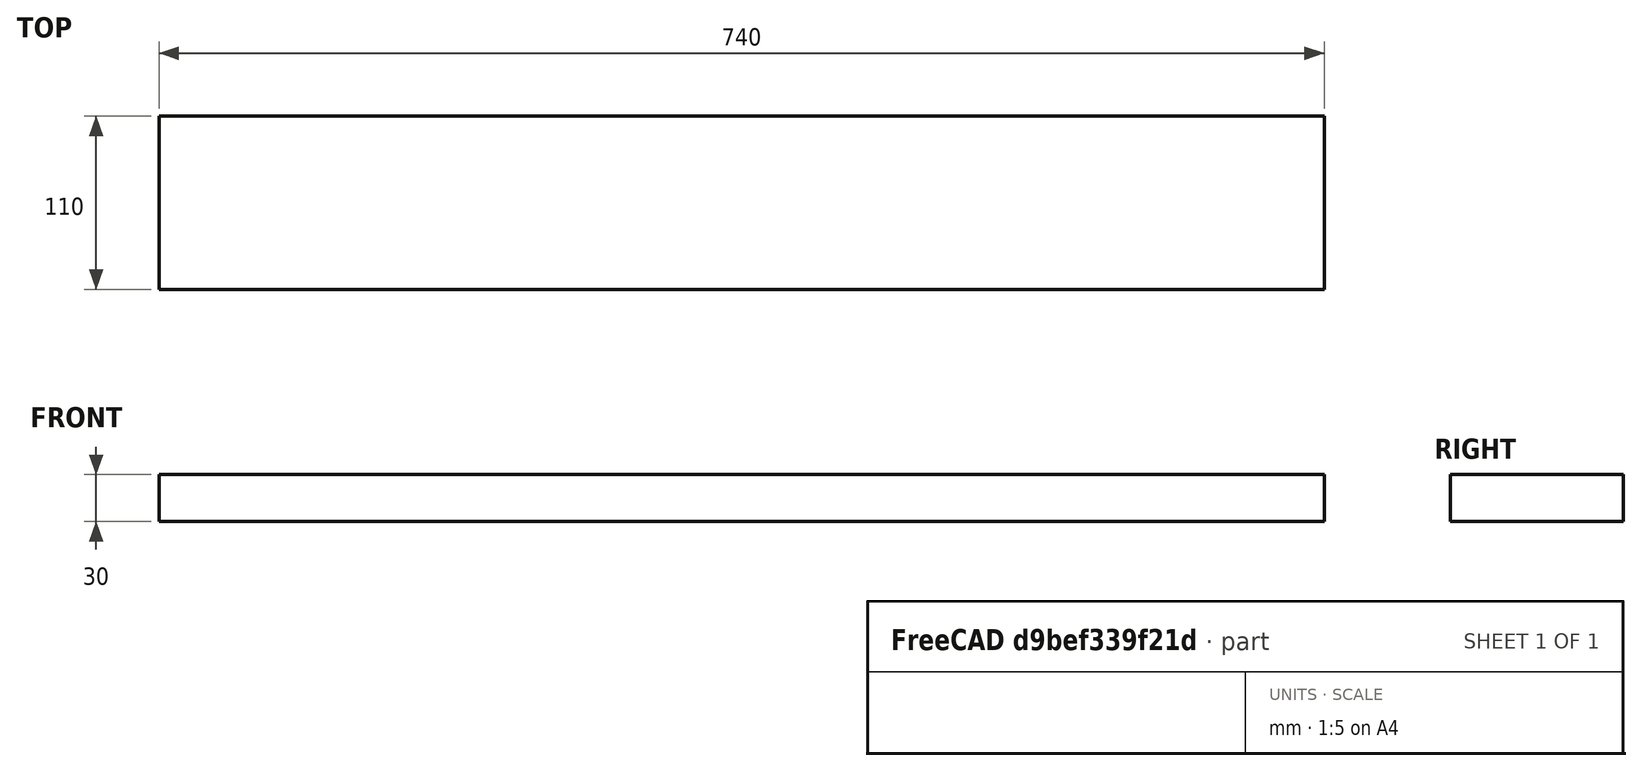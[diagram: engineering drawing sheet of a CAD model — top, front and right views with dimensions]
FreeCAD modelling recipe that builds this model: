
FCSTD DOCUMENT  (FreeCAD 1.0R39109 (Git))
Label: 025_table_frame_side_left
License: All rights reserved
LicenseURL: http://en.wikipedia.org/wiki/All_rights_reserved
objects: Spreadsheet::Sheet×1, Sketcher::SketchObject×1, PartDesign::Pad×1, PartDesign::Body×1
note: 6 computed .brp shape members not serialized (recipe doc carries the construction recipe); baked Part::Feature solids carry a one-line shape summary decoded from their .brp

FEATURE [Spreadsheet::Sheet] Spreadsheet
  cells = A4='length; B4(length)=800; A5='width; B5(width)=110; A6='height; B6(height)=30
FEATURE [Sketcher::SketchObject] Sketch
  ArcFitTolerance = 1e-06
  AttachmentSupport = -> [XY_Plane]
  FullyConstrained = true
  MakeInternals = false
  MapMode = 5
  expr: Constraints[11] = Spreadsheet.length - 2 * Spreadsheet.height
  expr: Constraints[12] = Spreadsheet.width
  sketch-geometry (5):
    g0: LineSegment StartX=-370 StartY=55 StartZ=0 EndX=-370 EndY=-55 EndZ=0
    g1: LineSegment StartX=-370 StartY=-55 StartZ=0 EndX=370 EndY=-55 EndZ=0
    g2: LineSegment StartX=370 StartY=-55 StartZ=0 EndX=370 EndY=55 EndZ=0
    g3: LineSegment StartX=370 StartY=55 StartZ=0 EndX=-370 EndY=55 EndZ=0
    g4: LineSegment [constr] StartX=-370 StartY=55 StartZ=0 EndX=370 EndY=-55 EndZ=0
  constraints (13):
    c: Coincident(g0,g1)
    c: Coincident(g1,g2)
    c: Coincident(g2,g3)
    c: Coincident(g3,g0)
    c: Vertical(g0)
    c: Vertical(g2)
    c: Horizontal(g1)
    c: Horizontal(g3)
    c: Coincident(g4,g0)
    c: Coincident(g4,g1)
    c: Symmetric(g4,g4,g-1)
    c: DistanceX(g3,g3) = 740
    c: DistanceY(g0,g0) = 110
FEATURE [PartDesign::Pad] Pad
  Direction = (0,0,1)
  Length = 30
  Length2 = 10
  Midplane = true
  Profile = -> Sketch
  ReferenceAxis = -> Sketch [N_Axis]
  Suppressed = false
  Type = 0
  expr: Length = Spreadsheet.height
FEATURE [PartDesign::Body] Body
  AllowCompound = false
  Group = -> [Sketch,Pad]
  Origin = -> Origin
  Tip = -> Pad
